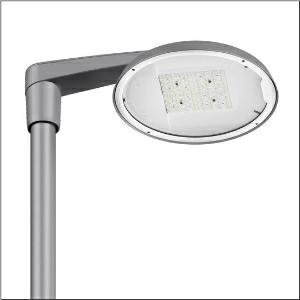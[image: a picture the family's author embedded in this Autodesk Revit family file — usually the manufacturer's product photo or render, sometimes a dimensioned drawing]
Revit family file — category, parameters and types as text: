
# Revit family: dl_r__50_iq_mini___st0_5a_5xa248b41f08le_50d6
name_source: partatom
category: Lighting Fixtures
units: mm (PartAtom-declared; Revit-internal decimal feet)

## family parameters
Cut with Voids When Loaded = No
Host = Face
Light Source = No
Part Type = Normal
Room Calculation Point = No
Round Connector Dimension = Use Diameter
Shared = No

## types (1)
- --- (1 x LED, 10390 lm, 64.1 W, 4000K)
    Apparent Load = 64 VA
    CIE Flux Codes = 41 75 97 100 100
    Color Rendering = 70
    Color Temperature = 4000K
    Default Elevation = 1800 mm
    Description = DL® 50 iQ mini, mast luminaire, primary light control with lens, of PMMA, primary optical cover: cover, of toughened safety glass, transparent, light distribution: ST0.5a, light emission: direct distribution, primary light characteristic: asymmetric, installation type: side-entry, post-top, LED, High Power LED, rated luminous flux: 10.390lm, luminous efficacy: 162lm/W, light colour: 740, colour temperature: 4000K, control: optimised constant luminous flux control (CLO 2.0), Desk-Remote (wireless, voltage-free reading and setting of iQ features in the workshop via application-optimized NFC function/RFID function), Light-Fading, Smart-Wire, Night-Set, Lumen-Switch, Temp-Guard, Auto-Match, Street-Remote, mains connection: 230..240V, AC, 50/60Hz, connection cable pre-assembled, cable length: 8,5m, start of lifetime: 64W, end of service life: 67W, reduction: 30W, luminaire housing, of diecast aluminium, powder-coated, Siteco® metallic grey (DB 702S), inclination adjustable: 0°, 5°, 10° (post-top) | 0°, -5°, -10°, -15° (side-entry), please order mast post-top element or mast side-entry element separately, diameter: 500mm, height: 115mm, post-top: for spigot size d x l = 76 x 100mm; with reducer (optional accessory) 60 x 100mm | side-entry: for spigot size d x l = 60 x 100mm; with reducer (optional accessory) 42 x 100mm, protection rating (complete): IP66, insulation class (complete): insulation class II (safety insulation), certification: CE, ENEC, VDE, impact resistance: IK08, permissible operating ambient temperature for outdoor applications: -25..+40°C, standard-compliant lighting for roads and squares, packaging unit: 1 piece

Light Distribution: ST0.5a
    Height = 115 mm
    Lamp = 1 x LED
    Lamp Light Flux = 10390 lm
    Lamp Power = 64.1 W
    Lamp count = 1
    Length = 500 mm
    Luminous efficacy = 162 lm/W
    Manufacturer = Siteco
    ModVariant = No
    Model = 5XA248B41F08LE
    Number of Poles = 1
    OnlyDefault = Yes
    Power Factor = 1
    Product Name = DL® 50 iQ mini | ST0.5a
    Product group = mast luminaire | pylon top
    ProductGroupID = 6100
    Protection Class = Protection class II
    Protection Degree = IP 66
    RLX_Detail_Level = 1
    RLX_Emergency_Light_Flux = 0 lm
    RLX_Emergency_Type = 0
    RLX_Emergency_Type_DB = No
    RlxData = <blob elided: 127853 chars, md5=450716ef>
    Socket = socket
    Standby Power = 0 W
    System Light Flux = 10390 lm
    System Power = 64 W
    Type Comments = factory setting: luminous flux: 100 % | dim-lin: 254 | 672 mA
    Type Image = l_1251790.jpg
    URL = http://relux.com
    VarID = @adj_092479
    Voltage = 0 V
    Weight = 0.00 kg
    Width = 0 mm  [stored 0 ft]

note: [stored X ft] marks values corroborated as IEEE doubles in the binary element streams (Revit-internal decimal feet)

## geometry (parser evidence)
native form markers: Blend x4, Sweep x10
no freeform markers — native parametric forms only
